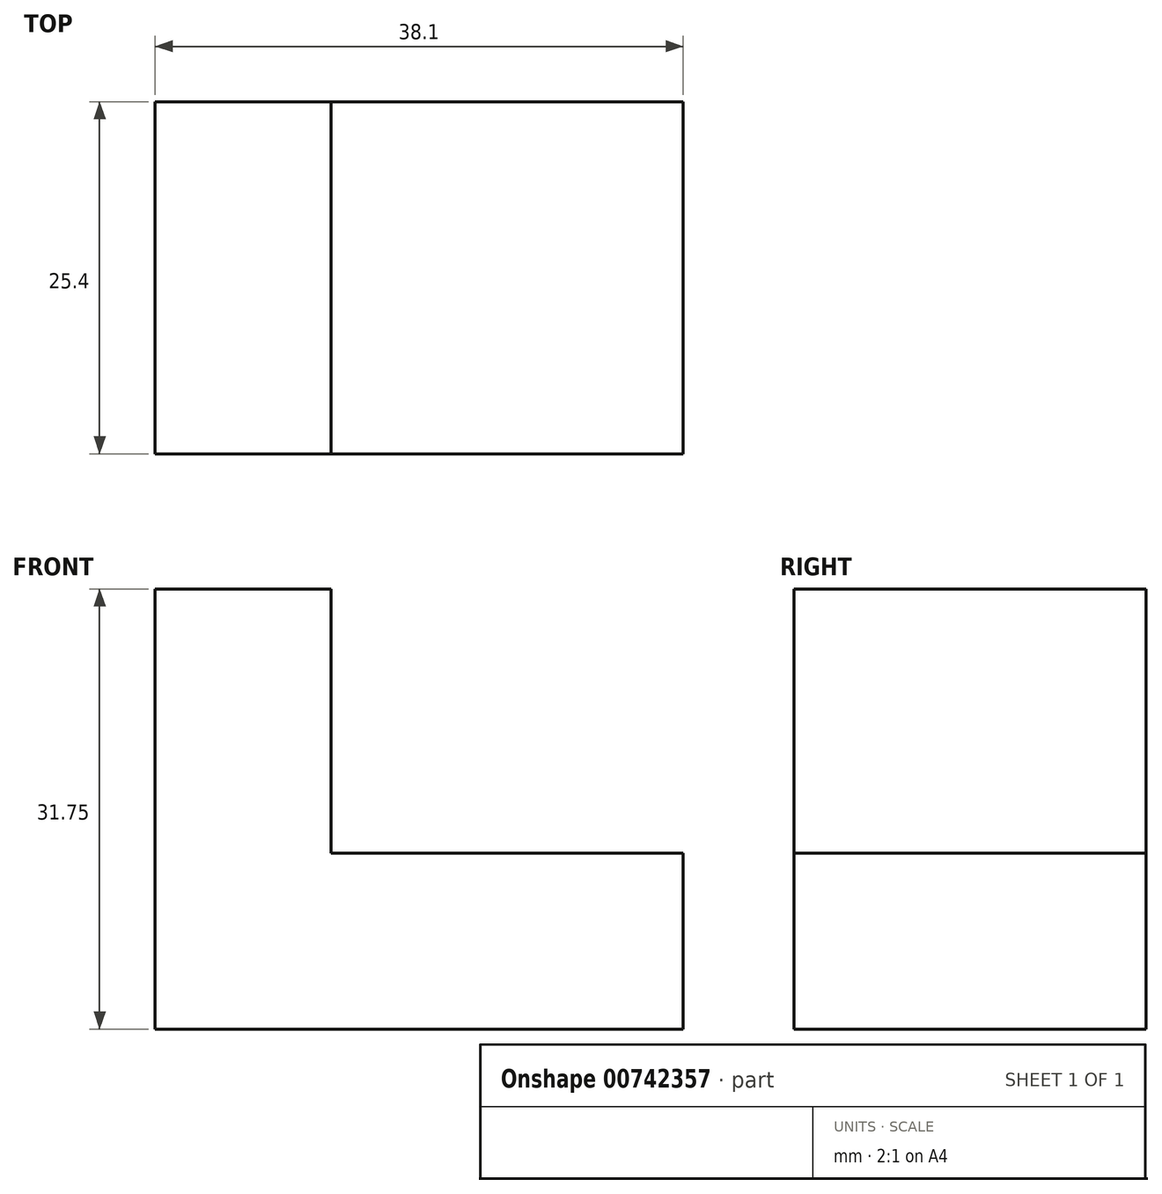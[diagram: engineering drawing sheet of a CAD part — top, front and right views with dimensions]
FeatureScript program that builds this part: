
annotation { "Feature Type Name" : "Feature", "Feature Type Description" : "" }
export const myFeature = defineFeature(function(context is Context, id is Id, definition is map)
    precondition{}
    {
        {
            var Q0;
            Q0=qCreatedBy(makeId("Front.planeOp"),FACE);
            var sketch = newSketch(context, id + "F0", { "sketchPlane" : qUnion([Q0])});
            skLineSegment(sketch, "E0", {"start": v(0, 31.75) * mm, "end": v(0, 0) * mm});
            skLineSegment(sketch, "E1", {"start": v(0, 0) * mm, "end": v(38.1, 0) * mm});
            skLineSegment(sketch, "E2", {"start": v(38.1, 12.7) * mm, "end": v(12.7, 12.7) * mm});
            skLineSegment(sketch, "E3", {"start": v(12.7, 12.7) * mm, "end": v(12.7, 31.75) * mm});
            skLineSegment(sketch, "E4", {"start": v(12.7, 31.75) * mm, "end": v(0, 31.75) * mm});
            skLineSegment(sketch, "E5", {"start": v(38.1, 12.7) * mm, "end": v(38.1, 0) * mm});
            skSolve(sketch);
        }
        {
            var Q0;
            Q0 = qSketchRegion(id + "F0", true);
            extrude(context, id + "F1", {"entities" : qUnion([Q0]), "depth" : 25.4 * mm, "offsetDistance" : 25.4 * mm});
        }
    });
